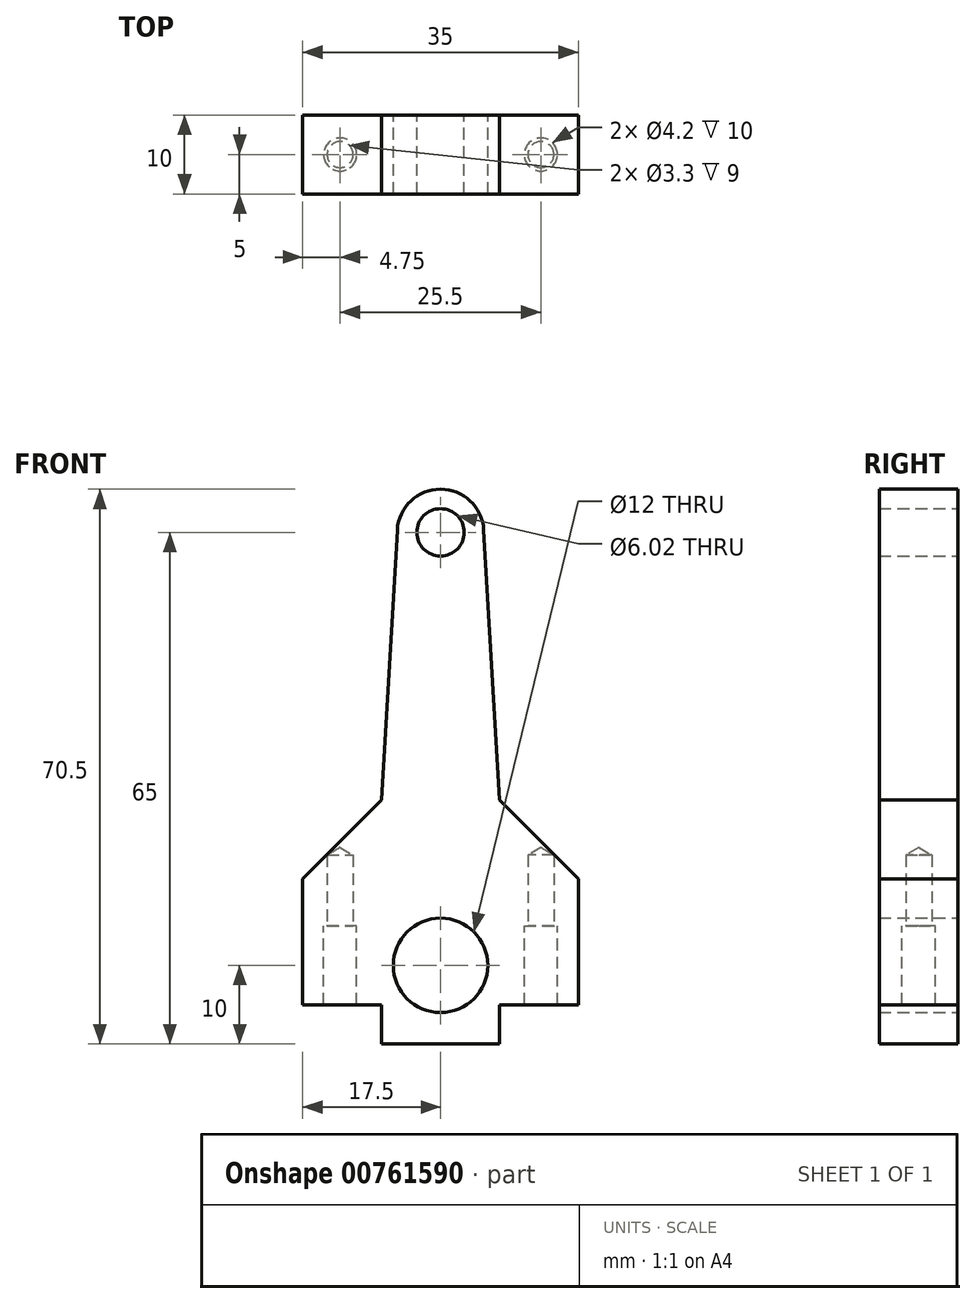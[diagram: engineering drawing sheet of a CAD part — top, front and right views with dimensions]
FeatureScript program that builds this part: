
annotation { "Feature Type Name" : "Feature", "Feature Type Description" : "" }
export const myFeature = defineFeature(function(context is Context, id is Id, definition is map)
    precondition{}
    {
        {
            var Q0;
            Q0=qCreatedBy(makeId("Front.planeOp"),FACE);
            var sketch = newSketch(context, id + "F0", { "sketchPlane" : qUnion([Q0])});
            skArc(sketch, "E0", {"start": v(-6, 0) * mm, "mid": v(-4.24, -4.24) * mm, "end": v(0, -6) * mm});
            skLineSegment(sketch, "E1", {"start": v(-6, 0) * mm, "end": v(-8, 0) * mm});
            skLineSegment(sketch, "E2", {"start": v(-8, 0) * mm, "end": v(-8, 5) * mm});
            skLineSegment(sketch, "E3", {"start": v(-8, 5) * mm, "end": v(-17.5, 5) * mm});
            skLineSegment(sketch, "E4", {"start": v(-17.5, 5) * mm, "end": v(-17.5, -5) * mm});
            skLineSegment(sketch, "E5", {"start": v(-17.5, -5) * mm, "end": v(-7.5, -5) * mm});
            skLineSegment(sketch, "E6", {"start": v(-7.5, -5) * mm, "end": v(-7.5, -10) * mm});
            skLineSegment(sketch, "E7", {"start": v(-7.5, -10) * mm, "end": v(0, -10) * mm});
            skLineSegment(sketch, "E8", {"start": v(0, -10) * mm, "end": v(0, -6) * mm});
            skSolve(sketch);
        }
        {
            var Q0;
            Q0 = qSketchRegion(id + "F0", true);
            extrude(context, id + "F1", {"entities" : qUnion([Q0]), "endBound" : BoundingType.SYMMETRIC, "depth" : 10 * mm, "offsetDistance" : 25 * mm});
        }
        {
            var Q0;
            Q0=qCreatedBy(makeId("Top.planeOp"),FACE);
            var sketch = newSketch(context, id + "F2", { "sketchPlane" : qUnion([Q0])});
            skCircle(sketch, "E9", {"center": v(-12.75, 0) * mm, "radius": 2.1 * mm});
            skSolve(sketch);
        }
        {
            var Q0;
            Q0 = qSketchRegion(id + "F2", true);
            extrude(context, id + "F3", {"entities" : qUnion([Q0]), "operationType" : NewBodyOperationType.REMOVE, "endBound" : BoundingType.SYMMETRIC, "oppositeDirection" : true, "depth" : 25 * mm, "offsetDistance" : 25 * mm});
        }
        {
            var Q0;
            Q0=makeQuery(id+"F1.opExtrude","SWEPT_BODY",BODY,{"disambiguationData":[OSD([sQuery(id+"F0.wireOp",EDGE,"E0"),sQuery(id+"F0.wireOp",EDGE,"E1"),sQuery(id+"F0.wireOp",EDGE,"E2"),sQuery(id+"F0.wireOp",EDGE,"E3"),sQuery(id+"F0.wireOp",EDGE,"E4"),sQuery(id+"F0.wireOp",EDGE,"E5"),sQuery(id+"F0.wireOp",EDGE,"E6"),sQuery(id+"F0.wireOp",EDGE,"E7"),sQuery(id+"F0.wireOp",EDGE,"E8")])]});
            var Q1;
            Q1=qCreatedBy(makeId("Right.planeOp"),FACE);
            mirror(context, id + "F4", {"operationType" : NewBodyOperationType.ADD, "entities" : qUnion([Q0]), "mirrorPlane" : qUnion([Q1])});
        }
        {
            var Q0;
            Q0=qCreatedBy(makeId("Front.planeOp"),FACE);
            var sketch = newSketch(context, id + "F5", { "sketchPlane" : qUnion([Q0])});
            skLineSegment(sketch, "E10.0", {"start": v(-6, 0) * mm, "end": v(-8, 0) * mm});
            skLineSegment(sketch, "E10.1", {"start": v(-8, 0) * mm, "end": v(-8, 5) * mm});
            skLineSegment(sketch, "E10.2", {"start": v(-8, 5) * mm, "end": v(-17.5, 5) * mm});
            skArc(sketch, "E11", {"start": v(0, 6) * mm, "mid": v(-4.24, 4.24) * mm, "end": v(-6, 0) * mm});
            skLineSegment(sketch, "E12", {"start": v(-17.5, 5) * mm, "end": v(-17.5, 11) * mm});
            skLineSegment(sketch, "E13", {"start": v(-17.5, 11) * mm, "end": v(-7.5, 21) * mm});
            skLineSegment(sketch, "E14", {"start": v(-7.5, 21) * mm, "end": v(-5.5, 55.32) * mm});
            skArc(sketch, "E15", {"start": v(0, 60.5) * mm, "mid": v(-3.77, 59) * mm, "end": v(-5.5, 55.32) * mm});
            skLineSegment(sketch, "E16", {"start": v(0, 60.5) * mm, "end": v(0, 58) * mm});
            skArc(sketch, "E17", {"start": v(0, 58) * mm, "mid": v(-3, 55) * mm, "end": v(0, 51.99) * mm});
            skLineSegment(sketch, "E18.trimOffspring", {"start": v(0, 51.99) * mm, "end": v(0, 6) * mm});
            skSolve(sketch);
        }
        {
            var Q0;
            Q0 = qSketchRegion(id + "F5", true);
            var Q1;
            {var subQ0=makeQuery(id+"F1.opExtrude","CAP_FACE",FACE,{"disambiguationData":[OSD([sQuery(id+"F0.wireOp",EDGE,"E0"),sQuery(id+"F0.wireOp",EDGE,"E1"),sQuery(id+"F0.wireOp",EDGE,"E2"),sQuery(id+"F0.wireOp",EDGE,"E3"),sQuery(id+"F0.wireOp",EDGE,"E4"),sQuery(id+"F0.wireOp",EDGE,"E5"),sQuery(id+"F0.wireOp",EDGE,"E6"),sQuery(id+"F0.wireOp",EDGE,"E7"),sQuery(id+"F0.wireOp",EDGE,"E8")])],"isStart":false});Q1=makeQuery(id+"F4.boolean.opBoolean","MERGE",FACE,{"derivedFrom":[subQ0,makeQuery(id+"F4.opPattern","COPY",FACE,{"derivedFrom":subQ0,"instanceName":"1"})]});}
            var Q2;
            {var subQ0=makeQuery(id+"F1.opExtrude","CAP_FACE",FACE,{"disambiguationData":[OSD([sQuery(id+"F0.wireOp",EDGE,"E0"),sQuery(id+"F0.wireOp",EDGE,"E1"),sQuery(id+"F0.wireOp",EDGE,"E2"),sQuery(id+"F0.wireOp",EDGE,"E3"),sQuery(id+"F0.wireOp",EDGE,"E4"),sQuery(id+"F0.wireOp",EDGE,"E5"),sQuery(id+"F0.wireOp",EDGE,"E6"),sQuery(id+"F0.wireOp",EDGE,"E7"),sQuery(id+"F0.wireOp",EDGE,"E8")])],"isStart":true});Q2=makeQuery(id+"F4.boolean.opBoolean","MERGE",FACE,{"derivedFrom":[subQ0,makeQuery(id+"F4.opPattern","COPY",FACE,{"derivedFrom":subQ0,"instanceName":"1"})]});}
            extrude(context, id + "F6", {"entities" : qUnion([Q0]), "endBound" : BoundingType.UP_TO_SURFACE, "depth" : 25 * mm, "endBoundEntityFace" : qUnion([Q1]), "offsetDistance" : 25 * mm, "hasSecondDirection" : true, "secondDirectionBound" : SecondDirectionBoundingType.UP_TO_SURFACE, "secondDirectionOppositeDirection" : true, "secondDirectionDepth" : 25 * mm, "secondDirectionBoundEntityFace" : qUnion([Q2])});
        }
        {
            var Q0;
            Q0=makeQuery(id+"F1.opExtrude","SWEPT_FACE",FACE,{"disambiguationData":[OSD([sQuery(id+"F0.wireOp",EDGE,"E3")])]});
            var sketch = newSketch(context, id + "F7", { "sketchPlane" : qUnion([Q0])});
            skPoint(sketch, "E19.0", {"position": v(-12.75, 0) * mm});
            skSolve(sketch);
        }
        {
            var Q0;
            Q0=sQuery(id+"F7.wireOp",VERTEX,"E19.0");
            var Q1;
            Q1=makeQuery(id+"F6.opExtrude","SWEPT_BODY",BODY,{"disambiguationData":[OSD([sQuery(id+"F5.wireOp",EDGE,"E10.0"),sQuery(id+"F5.wireOp",EDGE,"E10.1"),sQuery(id+"F5.wireOp",EDGE,"E10.2"),sQuery(id+"F5.wireOp",EDGE,"E11"),sQuery(id+"F5.wireOp",EDGE,"E12"),sQuery(id+"F5.wireOp",EDGE,"E13"),sQuery(id+"F5.wireOp",EDGE,"E14"),sQuery(id+"F5.wireOp",EDGE,"E15"),sQuery(id+"F5.wireOp",EDGE,"E16"),sQuery(id+"F5.wireOp",EDGE,"E17"),sQuery(id+"F5.wireOp",EDGE,"E18.trimOffspring")])]});
            hole(context, id + "F8", {"style" : HoleStyle.SIMPLE, "endStyle" : HoleEndStyle.BLIND, "oppositeDirection" : true, "standardTappedOrClearance" : lookupTablePath({ "standard" : "ISO", "engagement" : "75%", "pitch" : "0.7 mm", "size" : "M4", "type" : "Tapped" }), "standardBlindInLast" : lookupTablePath({ "standard" : "ISO", "engagement" : "75%", "pitch" : "0.7 mm", "size" : "M4", "type" : "Tapped" }), "holeDiameter" : 3.3 * mm, "majorDiameter" : 4 * mm, "showTappedDepth" : true, "holeDepth" : 9 * mm, "tappedDepth" : 5.5 * mm, "tapClearance" : 5, "startFromSketch" : true, "locations" : qUnion([Q0]), "scope" : qUnion([Q1])});
        }
        {
            var Q0;
            Q0=makeQuery(id+"F6.opExtrude","SWEPT_BODY",BODY,{"disambiguationData":[OSD([sQuery(id+"F5.wireOp",EDGE,"E10.0"),sQuery(id+"F5.wireOp",EDGE,"E10.1"),sQuery(id+"F5.wireOp",EDGE,"E10.2"),sQuery(id+"F5.wireOp",EDGE,"E11"),sQuery(id+"F5.wireOp",EDGE,"E12"),sQuery(id+"F5.wireOp",EDGE,"E13"),sQuery(id+"F5.wireOp",EDGE,"E14"),sQuery(id+"F5.wireOp",EDGE,"E15"),sQuery(id+"F5.wireOp",EDGE,"E16"),sQuery(id+"F5.wireOp",EDGE,"E17"),sQuery(id+"F5.wireOp",EDGE,"E18.trimOffspring")])]});
            var Q1;
            Q1=qCreatedBy(makeId("Right.planeOp"),FACE);
            mirror(context, id + "F9", {"operationType" : NewBodyOperationType.ADD, "entities" : qUnion([Q0]), "mirrorPlane" : qUnion([Q1])});
        }
    });
